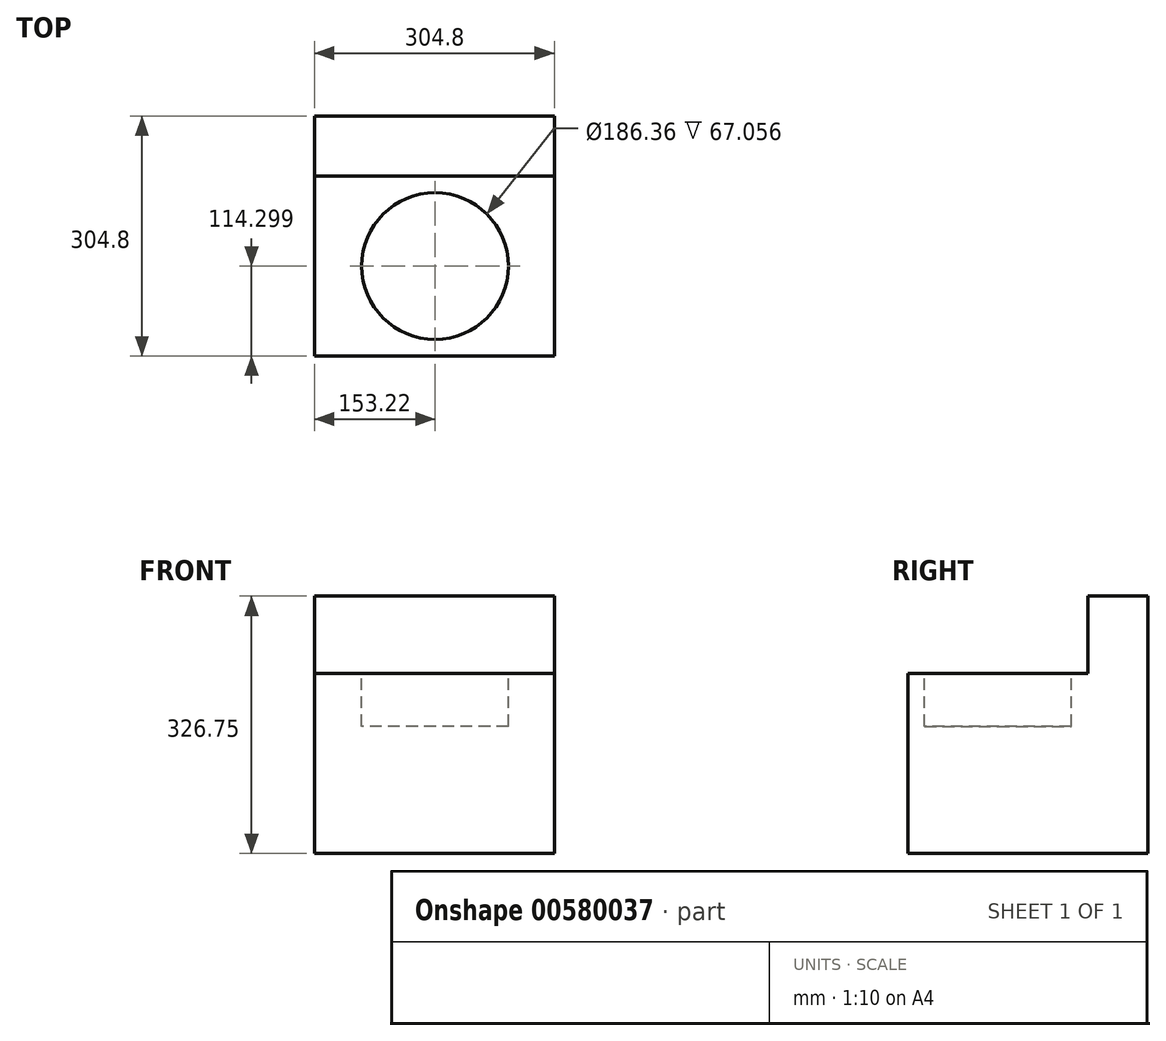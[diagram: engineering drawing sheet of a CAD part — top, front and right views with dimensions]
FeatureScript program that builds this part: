
annotation { "Feature Type Name" : "Feature", "Feature Type Description" : "" }
export const myFeature = defineFeature(function(context is Context, id is Id, definition is map)
    precondition{}
    {
        {
            var Q0;
            Q0=qCreatedBy(makeId("Top.planeOp"),FACE);
            var sketch = newSketch(context, id + "F0", { "sketchPlane" : qUnion([Q0])});
            skLineSegment(sketch, "E0.bottom", {"start": v(-223.22, 159.02) * mm, "end": v(81.58, 159.02) * mm});
            skLineSegment(sketch, "E0.top", {"start": v(-223.22, -145.78) * mm, "end": v(81.58, -145.78) * mm});
            skLineSegment(sketch, "E0.left", {"start": v(-223.22, 159.02) * mm, "end": v(-223.22, -145.78) * mm});
            skLineSegment(sketch, "E0.right", {"start": v(81.58, 159.02) * mm, "end": v(81.58, -145.78) * mm});
            skSolve(sketch);
        }
        {
            var Q0;
            Q0 = qSketchRegion(id + "F0", true);
            extrude(context, id + "F1", {"entities" : qUnion([Q0]), "depth" : 228.6 * mm, "offsetDistance" : 30.48 * mm});
        }
        {
            var Q0;
            Q0=makeQuery(id+"F1.opExtrude","CAP_FACE",FACE,{"disambiguationData":[OSD([sQuery(id+"F0.wireOp",EDGE,"E0.bottom"),sQuery(id+"F0.wireOp",EDGE,"E0.top"),sQuery(id+"F0.wireOp",EDGE,"E0.left"),sQuery(id+"F0.wireOp",EDGE,"E0.right")])],"isStart":false});
            var sketch = newSketch(context, id + "F2", { "sketchPlane" : qUnion([Q0])});
            skLineSegment(sketch, "E1.bottom", {"start": v(-223.22, 159.02) * mm, "end": v(81.58, 159.02) * mm});
            skLineSegment(sketch, "E1.top", {"start": v(-223.22, 82.82) * mm, "end": v(81.58, 82.82) * mm});
            skLineSegment(sketch, "E1.left", {"start": v(-223.22, 159.02) * mm, "end": v(-223.22, 82.82) * mm});
            skLineSegment(sketch, "E1.right", {"start": v(81.58, 159.02) * mm, "end": v(81.58, 82.82) * mm});
            skSolve(sketch);
        }
        {
            var Q0;
            Q0 = qSketchRegion(id + "F2", true);
            extrude(context, id + "F3", {"entities" : qUnion([Q0]), "operationType" : NewBodyOperationType.ADD, "depth" : 98.15 * mm, "offsetDistance" : 30.48 * mm});
        }
        {
            var Q0;
            Q0=makeQuery(id+"F1.opExtrude","CAP_FACE",FACE,{"disambiguationData":[OSD([sQuery(id+"F0.wireOp",EDGE,"E0.bottom"),sQuery(id+"F0.wireOp",EDGE,"E0.top"),sQuery(id+"F0.wireOp",EDGE,"E0.left"),sQuery(id+"F0.wireOp",EDGE,"E0.right")])],"isStart":false});
            var sketch = newSketch(context, id + "F4", { "sketchPlane" : qUnion([Q0])});
            skCircle(sketch, "E2", {"center": v(-70, -31.48) * mm, "radius": 93.18 * mm});
            skPoint(sketch, "E2.centerSnap0", {"position": v(-223.22, -31.48) * mm});
            skSolve(sketch);
        }
        {
            var Q0;
            Q0 = qSketchRegion(id + "F4", true);
            extrude(context, id + "F5", {"entities" : qUnion([Q0]), "operationType" : NewBodyOperationType.REMOVE, "oppositeDirection" : true, "depth" : 67.06 * mm, "offsetDistance" : 30.48 * mm});
        }
    });
